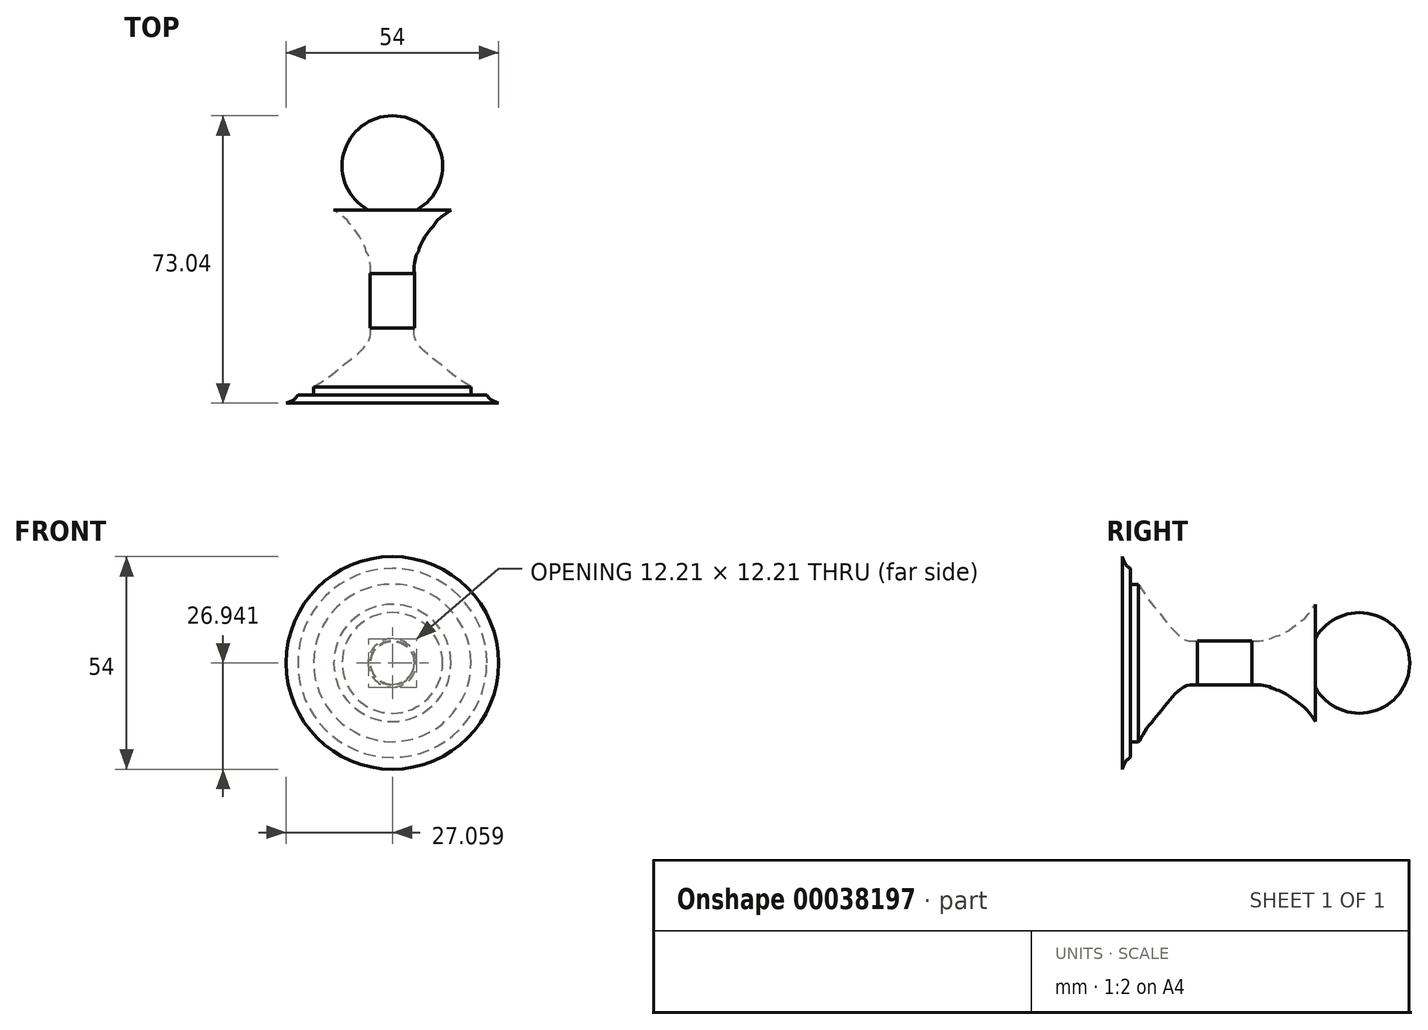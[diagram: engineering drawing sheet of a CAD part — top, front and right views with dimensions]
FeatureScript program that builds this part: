
annotation { "Feature Type Name" : "Feature", "Feature Type Description" : "" }
export const myFeature = defineFeature(function(context is Context, id is Id, definition is map)
    precondition{}
    {
        {
            var Q0;
            Q0=qCreatedBy(makeId("Top.planeOp"),FACE);
            var sketch = newSketch(context, id + "F0", { "sketchPlane" : qUnion([Q0])});
            skArc(sketch, "E0", {"start": v(6.17, 52.68) * mm, "mid": v(12.37, 67.04) * mm, "end": v(0, 76.63) * mm});
            skLineSegment(sketch, "E1", {"start": v(0, 63.86) * mm, "end": v(0, 3.59) * mm});
            skLineSegment(sketch, "E2", {"start": v(0, 63.86) * mm, "end": v(0, 52.68) * mm});
            skLineSegment(sketch, "E3", {"start": v(6.17, 52.68) * mm, "end": v(14.9, 52.68) * mm});
            skLineSegment(sketch, "E4", {"start": v(0, 52.68) * mm, "end": v(0, 36.48) * mm});
            skLineSegment(sketch, "E5", {"start": v(5.6, 36.48) * mm, "end": v(5.6, 22.68) * mm});
            skLineSegment(sketch, "E6", {"start": v(0, 22.68) * mm, "end": v(0, 7.68) * mm});
            skLineSegment(sketch, "E7", {"start": v(0, 7.68) * mm, "end": v(20, 7.68) * mm});
            skLineSegment(sketch, "E8", {"start": v(0, 7.68) * mm, "end": v(0, 5.68) * mm});
            skLineSegment(sketch, "E9", {"start": v(0, 5.68) * mm, "end": v(24, 5.68) * mm});
            skLineSegment(sketch, "E10", {"start": v(0, 5.68) * mm, "end": v(0, 3.59) * mm});
            skLineSegment(sketch, "E11", {"start": v(0, 3.59) * mm, "end": v(27, 3.59) * mm});
            skLineSegment(sketch, "E12", {"start": v(0, 63.86) * mm, "end": v(0, 76.63) * mm});
            skPoint(sketch, "E13.orphan", {"position": v(5.6, 21.48) * mm});
            skFitSpline(sketch, "E14", {"points": [v(14.9, 52.68) * mm, v(11.56, 50.17) * mm, v(10.48, 48.75) * mm, v(8.47, 46.16) * mm, v(7.47, 44.33) * mm, v(6.97, 43.4) * mm, v(6.72, 42.4) * mm, v(6.05, 40.99) * mm, v(5.72, 39.49) * mm, v(5.55, 38.32) * mm, v(5.6, 36.48) * mm], "startDerivative": vector(-26.16, -17.8) * mm, "endDerivative": vector(1.19, -19.71) * mm});
            skLineSegment(sketch, "E15", {"start": v(20, 7.68) * mm, "end": v(20, 5.68) * mm});
            skFitSpline(sketch, "E16", {"points": [v(27.76, 6.2) * mm, v(28.57, 5.56) * mm], "startDerivative": vector(0.81, -0.65) * mm, "endDerivative": vector(0.81, -0.65) * mm});
            skFitSpline(sketch, "E17", {"points": [v(24, 5.68) * mm, v(24.48, 5) * mm, v(25.21, 4.38) * mm, v(25.57, 4.21) * mm, v(26.19, 3.93) * mm, v(27, 3.59) * mm], "startDerivative": vector(2.3, -3.82) * mm, "endDerivative": vector(3.55, -1.97) * mm});
            skFitSpline(sketch, "E18", {"points": [v(5.6, 22.68) * mm, v(5.6, 20.5) * mm, v(6.46, 18.65) * mm, v(8.45, 16.53) * mm, v(10.62, 14.67) * mm, v(13.32, 12.55) * mm, v(15.26, 10.91) * mm, v(17.38, 9.37) * mm, v(19.42, 8.13) * mm, v(20, 7.68) * mm], "startDerivative": vector(-1.74, -20.94) * mm, "endDerivative": vector(7.67, -6.53) * mm});
            skSolve(sketch);
        }
        {
            var Q0;
            Q0 = qSketchRegion(id + "F0", true);
            var Q1;
            Q1=makeQuery(id+"F0.imprint","IMPRINT",FACE,{"disambiguationData":[TD([[makeQuery(id+"F0.imprint","IMPRINT",EDGE,{"derivedFrom":sQuery(id+"F0.wireOp",EDGE,"E0")}),1.0]])]});
            var Q2;
            Q2=sQuery(id+"F0.wireOp",EDGE,"E12");
            revolve(context, id + "F1", {"entities" : qUnion([Q0, Q1]), "axis" : qUnion([Q2]), "revolveType" : RevolveType.FULL});
        }
    });
